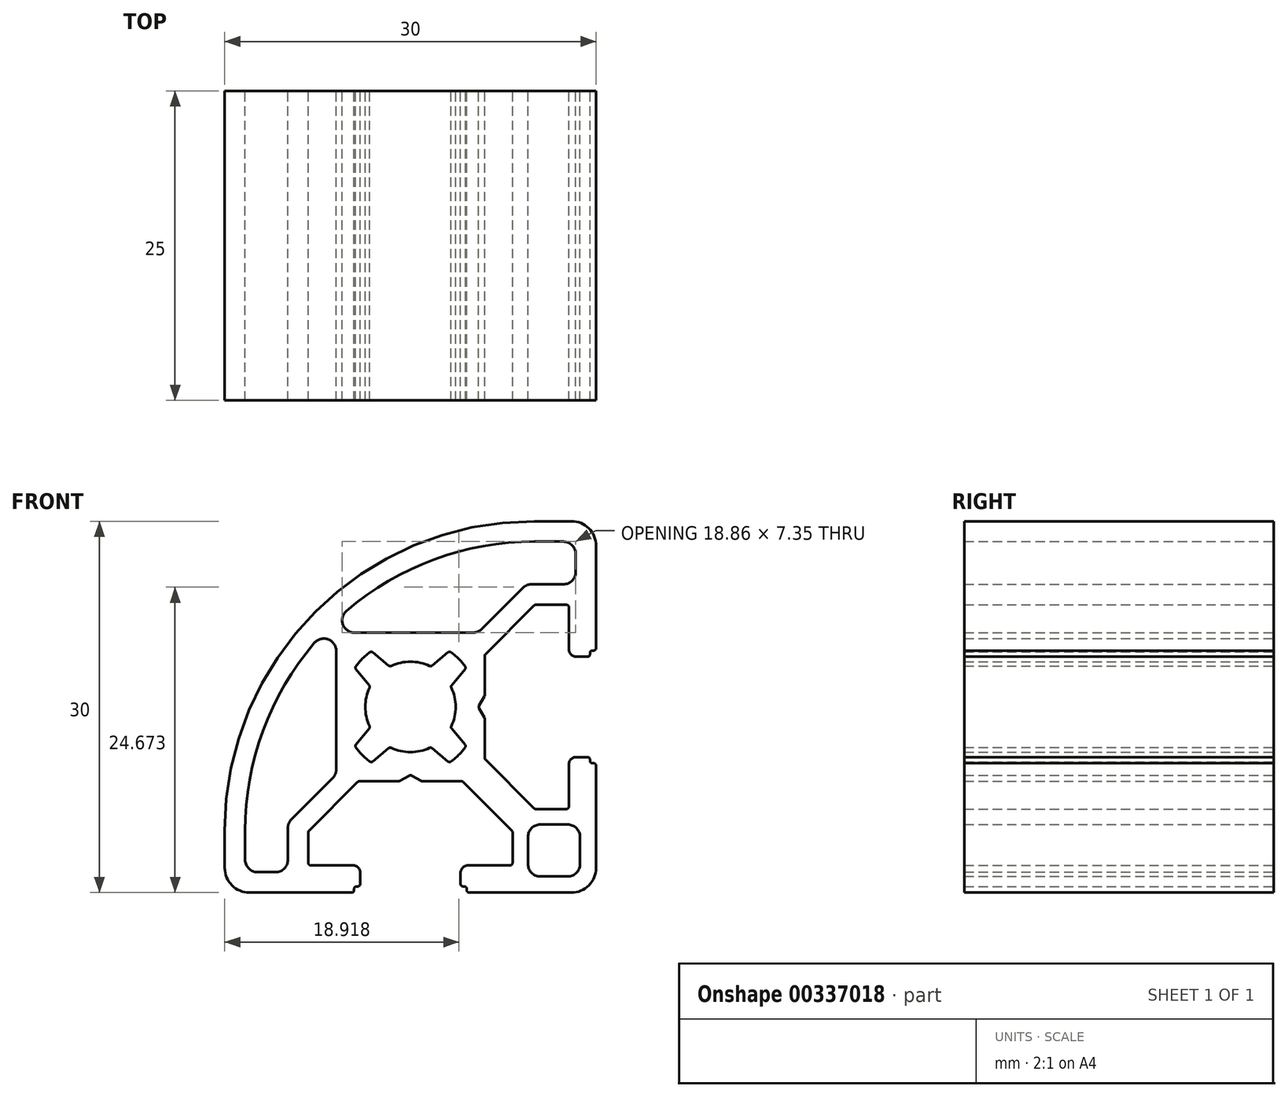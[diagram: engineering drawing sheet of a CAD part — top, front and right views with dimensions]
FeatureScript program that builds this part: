
annotation { "Feature Type Name" : "Feature", "Feature Type Description" : "" }
export const myFeature = defineFeature(function(context is Context, id is Id, definition is map)
    precondition{}
    {
        {
            var Q0;
            Q0=qCreatedBy(makeId("Front.planeOp"),FACE);
            var sketch = newSketch(context, id + "F0", { "sketchPlane" : qUnion([Q0])});
            skArc(sketch, "E0", {"start": v(-8.2, -10) * mm, "mid": v(-8.23, -10.06) * mm, "end": v(-8.25, -10.13) * mm});
            skLineSegment(sketch, "E1", {"start": v(-8.2, -10) * mm, "end": v(-4.26, -6.06) * mm});
            skArc(sketch, "E2", {"start": v(-4.12, -6) * mm, "mid": v(-4.2, -6.02) * mm, "end": v(-4.26, -6.06) * mm});
            skLineSegment(sketch, "E3", {"start": v(-4.12, -6) * mm, "end": v(-0.95, -6) * mm});
            skArc(sketch, "E4", {"start": v(-0.95, -6) * mm, "mid": v(-0.9, -6) * mm, "end": v(-0.85, -5.98) * mm});
            skLineSegment(sketch, "E5", {"start": v(-0.85, -5.98) * mm, "end": v(-0.1, -5.54) * mm});
            skArc(sketch, "E6", {"start": v(0.1, -5.54) * mm, "mid": v(0, -5.52) * mm, "end": v(-0.1, -5.54) * mm});
            skLineSegment(sketch, "E7", {"start": v(0.1, -5.54) * mm, "end": v(0.85, -5.98) * mm});
            skArc(sketch, "E8", {"start": v(0.85, -5.98) * mm, "mid": v(0.9, -6) * mm, "end": v(0.95, -6) * mm});
            skLineSegment(sketch, "E9", {"start": v(0.95, -6) * mm, "end": v(4.12, -6) * mm});
            skArc(sketch, "E10", {"start": v(4.26, -6.06) * mm, "mid": v(4.2, -6.02) * mm, "end": v(4.12, -6) * mm});
            skLineSegment(sketch, "E11", {"start": v(4.26, -6.06) * mm, "end": v(8.2, -10) * mm});
            skArc(sketch, "E12", {"start": v(8.25, -10.13) * mm, "mid": v(8.23, -10.06) * mm, "end": v(8.2, -10) * mm});
            skLineSegment(sketch, "E13", {"start": v(8.25, -10.13) * mm, "end": v(8.25, -12.6) * mm});
            skArc(sketch, "E14", {"start": v(8.05, -12.8) * mm, "mid": v(8.2, -12.74) * mm, "end": v(8.25, -12.6) * mm});
            skLineSegment(sketch, "E15", {"start": v(8.05, -12.8) * mm, "end": v(4.65, -12.8) * mm});
            skArc(sketch, "E16", {"start": v(4.65, -12.8) * mm, "mid": v(4.23, -12.98) * mm, "end": v(4.05, -13.4) * mm});
            skLineSegment(sketch, "E17", {"start": v(4.05, -13.4) * mm, "end": v(4.05, -14.3) * mm});
            skArc(sketch, "E18", {"start": v(4.05, -14.3) * mm, "mid": v(4.1, -14.44) * mm, "end": v(4.25, -14.5) * mm});
            skLineSegment(sketch, "E19", {"start": v(4.25, -14.5) * mm, "end": v(4.35, -14.5) * mm});
            skArc(sketch, "E20", {"start": v(4.55, -14.7) * mm, "mid": v(4.5, -14.56) * mm, "end": v(4.35, -14.5) * mm});
            skLineSegment(sketch, "E21", {"start": v(4.55, -14.7) * mm, "end": v(4.55, -14.8) * mm});
            skArc(sketch, "E22", {"start": v(4.55, -14.8) * mm, "mid": v(4.6, -14.94) * mm, "end": v(4.75, -15) * mm});
            skLineSegment(sketch, "E23", {"start": v(4.75, -15) * mm, "end": v(13, -15) * mm});
            skArc(sketch, "E24", {"start": v(13, -15) * mm, "mid": v(14.41, -14.41) * mm, "end": v(15, -13) * mm});
            skLineSegment(sketch, "E25", {"start": v(15, -13) * mm, "end": v(15, -4.75) * mm});
            skArc(sketch, "E26", {"start": v(15, -4.75) * mm, "mid": v(14.94, -4.6) * mm, "end": v(14.8, -4.55) * mm});
            skLineSegment(sketch, "E27", {"start": v(14.8, -4.55) * mm, "end": v(14.7, -4.55) * mm});
            skArc(sketch, "E28", {"start": v(14.5, -4.35) * mm, "mid": v(14.56, -4.5) * mm, "end": v(14.7, -4.55) * mm});
            skLineSegment(sketch, "E29", {"start": v(14.5, -4.35) * mm, "end": v(14.5, -4.25) * mm});
            skArc(sketch, "E30", {"start": v(14.5, -4.25) * mm, "mid": v(14.44, -4.1) * mm, "end": v(14.3, -4.05) * mm});
            skLineSegment(sketch, "E31", {"start": v(14.3, -4.05) * mm, "end": v(13.4, -4.05) * mm});
            skArc(sketch, "E32", {"start": v(13.4, -4.05) * mm, "mid": v(12.98, -4.23) * mm, "end": v(12.8, -4.65) * mm});
            skLineSegment(sketch, "E33", {"start": v(12.8, -4.65) * mm, "end": v(12.8, -8.05) * mm});
            skArc(sketch, "E34", {"start": v(12.6, -8.25) * mm, "mid": v(12.74, -8.2) * mm, "end": v(12.8, -8.05) * mm});
            skLineSegment(sketch, "E35", {"start": v(12.6, -8.25) * mm, "end": v(10.13, -8.25) * mm});
            skArc(sketch, "E36", {"start": v(10, -8.2) * mm, "mid": v(10.06, -8.23) * mm, "end": v(10.13, -8.25) * mm});
            skLineSegment(sketch, "E37", {"start": v(10, -8.2) * mm, "end": v(6.06, -4.26) * mm});
            skArc(sketch, "E38", {"start": v(6, -4.12) * mm, "mid": v(6.02, -4.2) * mm, "end": v(6.06, -4.26) * mm});
            skLineSegment(sketch, "E39", {"start": v(6, -4.12) * mm, "end": v(6, -0.95) * mm});
            skArc(sketch, "E40", {"start": v(6, -0.95) * mm, "mid": v(6, -0.9) * mm, "end": v(5.98, -0.85) * mm});
            skLineSegment(sketch, "E41", {"start": v(5.98, -0.85) * mm, "end": v(5.54, -0.1) * mm});
            skArc(sketch, "E42", {"start": v(5.54, 0.1) * mm, "mid": v(5.52, 0) * mm, "end": v(5.54, -0.1) * mm});
            skLineSegment(sketch, "E43", {"start": v(5.54, 0.1) * mm, "end": v(5.98, 0.85) * mm});
            skArc(sketch, "E44", {"start": v(5.98, 0.85) * mm, "mid": v(6, 0.9) * mm, "end": v(6, 0.95) * mm});
            skLineSegment(sketch, "E45", {"start": v(6, 0.95) * mm, "end": v(6, 4.12) * mm});
            skArc(sketch, "E46", {"start": v(6.06, 4.26) * mm, "mid": v(6.02, 4.2) * mm, "end": v(6, 4.12) * mm});
            skLineSegment(sketch, "E47", {"start": v(6.06, 4.26) * mm, "end": v(10, 8.2) * mm});
            skArc(sketch, "E48", {"start": v(10.13, 8.25) * mm, "mid": v(10.06, 8.23) * mm, "end": v(10, 8.2) * mm});
            skLineSegment(sketch, "E49", {"start": v(10.13, 8.25) * mm, "end": v(12.6, 8.25) * mm});
            skArc(sketch, "E50", {"start": v(12.8, 8.05) * mm, "mid": v(12.74, 8.2) * mm, "end": v(12.6, 8.25) * mm});
            skLineSegment(sketch, "E51", {"start": v(12.8, 8.05) * mm, "end": v(12.8, 4.65) * mm});
            skArc(sketch, "E52", {"start": v(12.8, 4.65) * mm, "mid": v(12.98, 4.23) * mm, "end": v(13.4, 4.05) * mm});
            skLineSegment(sketch, "E53", {"start": v(13.4, 4.05) * mm, "end": v(14.3, 4.05) * mm});
            skArc(sketch, "E54", {"start": v(14.3, 4.05) * mm, "mid": v(14.44, 4.1) * mm, "end": v(14.5, 4.25) * mm});
            skLineSegment(sketch, "E55", {"start": v(14.5, 4.25) * mm, "end": v(14.5, 4.35) * mm});
            skArc(sketch, "E56", {"start": v(14.7, 4.55) * mm, "mid": v(14.56, 4.5) * mm, "end": v(14.5, 4.35) * mm});
            skLineSegment(sketch, "E57", {"start": v(14.7, 4.55) * mm, "end": v(14.8, 4.55) * mm});
            skArc(sketch, "E58", {"start": v(14.8, 4.55) * mm, "mid": v(14.94, 4.6) * mm, "end": v(15, 4.75) * mm});
            skLineSegment(sketch, "E59", {"start": v(15, 4.75) * mm, "end": v(15, 13) * mm});
            skArc(sketch, "E60", {"start": v(15, 13) * mm, "mid": v(14.41, 14.41) * mm, "end": v(13, 15) * mm});
            skLineSegment(sketch, "E61", {"start": v(13, 15) * mm, "end": v(10, 15) * mm});
            skArc(sketch, "E62", {"start": v(10, 15) * mm, "mid": v(-7.68, 7.68) * mm, "end": v(-15, -10) * mm});
            skLineSegment(sketch, "E63", {"start": v(-15, -10) * mm, "end": v(-15, -13) * mm});
            skArc(sketch, "E64", {"start": v(-15, -13) * mm, "mid": v(-14.41, -14.41) * mm, "end": v(-13, -15) * mm});
            skLineSegment(sketch, "E65", {"start": v(-13, -15) * mm, "end": v(-4.75, -15) * mm});
            skArc(sketch, "E66", {"start": v(-4.75, -15) * mm, "mid": v(-4.6, -14.94) * mm, "end": v(-4.55, -14.8) * mm});
            skLineSegment(sketch, "E67", {"start": v(-4.55, -14.8) * mm, "end": v(-4.55, -14.7) * mm});
            skArc(sketch, "E68", {"start": v(-4.35, -14.5) * mm, "mid": v(-4.5, -14.56) * mm, "end": v(-4.55, -14.7) * mm});
            skLineSegment(sketch, "E69", {"start": v(-4.35, -14.5) * mm, "end": v(-4.25, -14.5) * mm});
            skArc(sketch, "E70", {"start": v(-4.25, -14.5) * mm, "mid": v(-4.1, -14.44) * mm, "end": v(-4.05, -14.3) * mm});
            skLineSegment(sketch, "E71", {"start": v(-4.05, -14.3) * mm, "end": v(-4.05, -13.4) * mm});
            skArc(sketch, "E72", {"start": v(-4.05, -13.4) * mm, "mid": v(-4.23, -12.98) * mm, "end": v(-4.65, -12.8) * mm});
            skLineSegment(sketch, "E73", {"start": v(-4.65, -12.8) * mm, "end": v(-8.05, -12.8) * mm});
            skArc(sketch, "E74", {"start": v(-8.25, -12.6) * mm, "mid": v(-8.2, -12.74) * mm, "end": v(-8.05, -12.8) * mm});
            skLineSegment(sketch, "E75", {"start": v(-8.25, -12.6) * mm, "end": v(-8.25, -10.13) * mm});
            skArc(sketch, "E76", {"start": v(-7.76, 5.16) * mm, "mid": v(-11.9, -1.92) * mm, "end": v(-13.35, -10) * mm});
            skArc(sketch, "E77", {"start": v(-6, 4.51) * mm, "mid": v(-6.65, 5.45) * mm, "end": v(-7.76, 5.16) * mm});
            skLineSegment(sketch, "E78", {"start": v(-6, -5.05) * mm, "end": v(-6, 4.51) * mm});
            skArc(sketch, "E79", {"start": v(-6.29, -5.75) * mm, "mid": v(-6.07, -5.43) * mm, "end": v(-6, -5.05) * mm});
            skLineSegment(sketch, "E80", {"start": v(-9.6, -9.07) * mm, "end": v(-6.29, -5.75) * mm});
            skArc(sketch, "E81", {"start": v(-9.6, -9.07) * mm, "mid": v(-9.82, -9.4) * mm, "end": v(-9.9, -9.78) * mm});
            skLineSegment(sketch, "E82", {"start": v(-9.9, -12.35) * mm, "end": v(-9.9, -9.78) * mm});
            skArc(sketch, "E83", {"start": v(-10.9, -13.35) * mm, "mid": v(-10.2, -13.06) * mm, "end": v(-9.9, -12.35) * mm});
            skLineSegment(sketch, "E84", {"start": v(-12.35, -13.35) * mm, "end": v(-10.9, -13.35) * mm});
            skArc(sketch, "E85", {"start": v(-13.35, -12.35) * mm, "mid": v(-13.06, -13.06) * mm, "end": v(-12.35, -13.35) * mm});
            skLineSegment(sketch, "E86", {"start": v(-13.35, -10) * mm, "end": v(-13.35, -12.35) * mm});
            skArc(sketch, "E87", {"start": v(-5.16, 7.76) * mm, "mid": v(-5.45, 6.65) * mm, "end": v(-4.51, 6) * mm});
            skArc(sketch, "E88", {"start": v(10, 13.35) * mm, "mid": v(1.92, 11.9) * mm, "end": v(-5.16, 7.76) * mm});
            skLineSegment(sketch, "E89", {"start": v(12.35, 13.35) * mm, "end": v(10, 13.35) * mm});
            skArc(sketch, "E90", {"start": v(13.35, 12.35) * mm, "mid": v(13.06, 13.06) * mm, "end": v(12.35, 13.35) * mm});
            skLineSegment(sketch, "E91", {"start": v(13.35, 10.9) * mm, "end": v(13.35, 12.35) * mm});
            skArc(sketch, "E92", {"start": v(12.35, 9.9) * mm, "mid": v(13.06, 10.2) * mm, "end": v(13.35, 10.9) * mm});
            skLineSegment(sketch, "E93", {"start": v(9.78, 9.9) * mm, "end": v(12.35, 9.9) * mm});
            skArc(sketch, "E94", {"start": v(9.78, 9.9) * mm, "mid": v(9.4, 9.82) * mm, "end": v(9.07, 9.6) * mm});
            skLineSegment(sketch, "E95", {"start": v(5.75, 6.29) * mm, "end": v(9.07, 9.6) * mm});
            skArc(sketch, "E96", {"start": v(5.05, 6) * mm, "mid": v(5.43, 6.07) * mm, "end": v(5.75, 6.29) * mm});
            skLineSegment(sketch, "E97", {"start": v(-4.51, 6) * mm, "end": v(5.05, 6) * mm});
            skArc(sketch, "E98", {"start": v(3.28, 4.41) * mm, "mid": v(3.16, 4.45) * mm, "end": v(3.04, 4.4) * mm});
            skArc(sketch, "E99", {"start": v(4.41, 3.28) * mm, "mid": v(3.89, 3.89) * mm, "end": v(3.28, 4.41) * mm});
            skArc(sketch, "E100", {"start": v(4.4, 3.04) * mm, "mid": v(4.45, 3.16) * mm, "end": v(4.41, 3.28) * mm});
            skLineSegment(sketch, "E101", {"start": v(3.33, 1.76) * mm, "end": v(4.4, 3.04) * mm});
            skArc(sketch, "E102", {"start": v(3.33, 1.76) * mm, "mid": v(3.29, 1.66) * mm, "end": v(3.3, 1.55) * mm});
            skArc(sketch, "E103", {"start": v(3.3, -1.55) * mm, "mid": v(3.65, 0) * mm, "end": v(3.3, 1.55) * mm});
            skArc(sketch, "E104", {"start": v(3.3, -1.55) * mm, "mid": v(3.29, -1.66) * mm, "end": v(3.33, -1.76) * mm});
            skLineSegment(sketch, "E105", {"start": v(4.4, -3.04) * mm, "end": v(3.33, -1.76) * mm});
            skArc(sketch, "E106", {"start": v(4.41, -3.28) * mm, "mid": v(4.45, -3.16) * mm, "end": v(4.4, -3.04) * mm});
            skArc(sketch, "E107", {"start": v(3.28, -4.41) * mm, "mid": v(3.89, -3.89) * mm, "end": v(4.41, -3.28) * mm});
            skArc(sketch, "E108", {"start": v(3.04, -4.4) * mm, "mid": v(3.16, -4.45) * mm, "end": v(3.28, -4.41) * mm});
            skLineSegment(sketch, "E109", {"start": v(1.76, -3.33) * mm, "end": v(3.04, -4.4) * mm});
            skArc(sketch, "E110", {"start": v(1.76, -3.33) * mm, "mid": v(1.66, -3.29) * mm, "end": v(1.55, -3.3) * mm});
            skArc(sketch, "E111", {"start": v(-1.55, -3.3) * mm, "mid": v(0, -3.65) * mm, "end": v(1.55, -3.3) * mm});
            skArc(sketch, "E112", {"start": v(-1.55, -3.3) * mm, "mid": v(-1.66, -3.29) * mm, "end": v(-1.76, -3.33) * mm});
            skLineSegment(sketch, "E113", {"start": v(-3.04, -4.4) * mm, "end": v(-1.76, -3.33) * mm});
            skArc(sketch, "E114", {"start": v(-3.28, -4.41) * mm, "mid": v(-3.16, -4.45) * mm, "end": v(-3.04, -4.4) * mm});
            skArc(sketch, "E115", {"start": v(-4.41, -3.28) * mm, "mid": v(-3.89, -3.89) * mm, "end": v(-3.28, -4.41) * mm});
            skArc(sketch, "E116", {"start": v(-4.4, -3.04) * mm, "mid": v(-4.45, -3.16) * mm, "end": v(-4.41, -3.28) * mm});
            skLineSegment(sketch, "E117", {"start": v(-3.33, -1.76) * mm, "end": v(-4.4, -3.04) * mm});
            skArc(sketch, "E118", {"start": v(-3.33, -1.76) * mm, "mid": v(-3.29, -1.66) * mm, "end": v(-3.3, -1.55) * mm});
            skArc(sketch, "E119", {"start": v(-3.3, 1.55) * mm, "mid": v(-3.65, 0) * mm, "end": v(-3.3, -1.55) * mm});
            skArc(sketch, "E120", {"start": v(-3.3, 1.55) * mm, "mid": v(-3.29, 1.66) * mm, "end": v(-3.33, 1.76) * mm});
            skLineSegment(sketch, "E121", {"start": v(-4.4, 3.04) * mm, "end": v(-3.33, 1.76) * mm});
            skArc(sketch, "E122", {"start": v(-4.41, 3.28) * mm, "mid": v(-4.45, 3.16) * mm, "end": v(-4.4, 3.04) * mm});
            skArc(sketch, "E123", {"start": v(-3.28, 4.41) * mm, "mid": v(-3.89, 3.89) * mm, "end": v(-4.41, 3.28) * mm});
            skArc(sketch, "E124", {"start": v(-3.04, 4.4) * mm, "mid": v(-3.16, 4.45) * mm, "end": v(-3.28, 4.41) * mm});
            skLineSegment(sketch, "E125", {"start": v(-1.76, 3.33) * mm, "end": v(-3.04, 4.4) * mm});
            skArc(sketch, "E126", {"start": v(-1.76, 3.33) * mm, "mid": v(-1.66, 3.29) * mm, "end": v(-1.55, 3.3) * mm});
            skArc(sketch, "E127", {"start": v(1.55, 3.3) * mm, "mid": v(0, 3.65) * mm, "end": v(-1.55, 3.3) * mm});
            skArc(sketch, "E128", {"start": v(1.55, 3.3) * mm, "mid": v(1.66, 3.29) * mm, "end": v(1.76, 3.33) * mm});
            skLineSegment(sketch, "E129", {"start": v(3.04, 4.4) * mm, "end": v(1.76, 3.33) * mm});
            skLineSegment(sketch, "E130", {"start": v(12.7, -9.5) * mm, "end": v(10.5, -9.5) * mm});
            skArc(sketch, "E131", {"start": v(13.7, -10.5) * mm, "mid": v(13.4, -9.8) * mm, "end": v(12.7, -9.5) * mm});
            skLineSegment(sketch, "E132", {"start": v(13.7, -12.7) * mm, "end": v(13.7, -10.5) * mm});
            skArc(sketch, "E133", {"start": v(12.7, -13.7) * mm, "mid": v(13.4, -13.4) * mm, "end": v(13.7, -12.7) * mm});
            skLineSegment(sketch, "E134", {"start": v(10.5, -13.7) * mm, "end": v(12.7, -13.7) * mm});
            skArc(sketch, "E135", {"start": v(9.5, -12.7) * mm, "mid": v(9.8, -13.4) * mm, "end": v(10.5, -13.7) * mm});
            skLineSegment(sketch, "E136", {"start": v(9.5, -10.5) * mm, "end": v(9.5, -12.7) * mm});
            skArc(sketch, "E137", {"start": v(10.5, -9.5) * mm, "mid": v(9.8, -9.8) * mm, "end": v(9.5, -10.5) * mm});
            skSolve(sketch);
        }
        {
            var Q0;
            Q0=makeQuery(id+"F0.imprint","IMPRINT",FACE,{"disambiguationData":[TD([[makeQuery(id+"F0.imprint","IMPRINT",EDGE,{"derivedFrom":sQuery(id+"F0.wireOp",EDGE,"E0")}),-1.0]])]});
            extrude(context, id + "F1", {"entities" : qUnion([Q0]), "depth" : 25 * mm});
        }
    });
